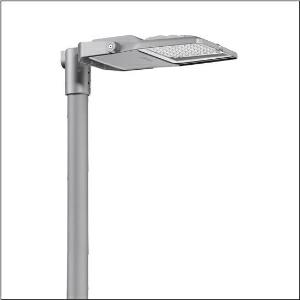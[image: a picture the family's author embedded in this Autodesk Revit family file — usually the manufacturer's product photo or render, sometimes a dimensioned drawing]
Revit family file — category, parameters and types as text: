
# Revit family: floodlight_fl_21_iq_mini___pl64_5xa7771b4e3a_3408
name_source: partatom
category: Lighting Fixtures
units: mm (PartAtom-declared; Revit-internal decimal feet)

## family parameters
Cut with Voids When Loaded = No
Host = Face
Light Source = No
Part Type = Normal
Room Calculation Point = No
Round Connector Dimension = Use Diameter
Shared = No

## types (1)
- --- (1 x LED, 6270 lm, 45.5 W, 4000K)
    Apparent Load = 46 VA
    CIE Flux Codes = 28 80 98 100 100
    Color Rendering = 70
    Color Temperature = 4000K
    Default Elevation = 1800 mm
    Description = Floodlight FL 21 iQ mini, floodlight, primary light control with lens, of PMMA, primary optical cover: protective disc, of toughened safety glass, transparent, light distribution: PL64, light emission: direct distribution, installation type: surface-mounted, LED, High Power LED, rated luminous flux: 6.270lm, luminous efficacy: 138lm/W, light colour: 740, colour temperature: 4000K, control: Auto-Match, Temp-Guard, Lumen-Switch, Night-Set, Smart-Wire, Light-Fading, Desk-Remote (wireless, voltage-free reading and setting of iQ features in the workshop via application-optimized NFC function/RFID function), optimised constant luminous flux control (CLO 2.0), with terminal, 6-pole, mains connection: 220..240V, AC, 50/60Hz, start of lifetime: 46W, end of service life: 48W, reduction: 22W, luminaire housing, of diecast aluminium, powder-coated, Siteco® metallic grey (DB 702S), corrosivity category C5 mid according to DIN EN ISO 12944, sealing non-destructively replaceable, please order mast flange separately, mast bracket, of steel, galvanised, powder-coated, Siteco® metallic grey (DB 702S), protection rating (complete): IP66, insulation class (complete): insulation class II (safety insulation), certification: CE, ENEC, VDE, protection symbol: D, impact resistance: IK08, permissible operating ambient temperature: -40..+40°C, permissible operating ambient temperature for outdoor applications: -40..+50°C, standard: DIN EN 12944, LABS conformity tested according to VDMA 24364:2018-05, packaging unit: 1 piece

Light Distribution: PL64
    Height = 70 mm
    Lamp = 1 x LED
    Lamp Light Flux = 6270 lm
    Lamp Power = 45.5 W
    Lamp count = 1
    Length = 485 mm
    Luminous efficacy = 138 lm/W
    Manufacturer = Siteco
    ModVariant = No
    Model = 5XA7771B4E3A
    Number of Poles = 1
    OnlyDefault = Yes
    Power Factor = 1
    Product Name = Floodlight FL 21 iQ mini | PL64
    Product group = floodlight | pylon annexe
    ProductGroupID = 6200
    Protection Class = Protection class II
    Protection Degree = IP 66
    RLX_Detail_Level = 1
    RLX_Emergency_Light_Flux = 0 lm
    RLX_Emergency_Type = 0
    RLX_Emergency_Type_DB = No
    RlxData = <blob elided: 101309 chars, md5=3e97cf1d>
    Socket = socket
    Standby Power = 0 W
    System Light Flux = 6270 lm
    System Power = 46 W
    Type Comments = factory setting: luminous flux: 100 % | dim-lin: 254 | 463 mA
    Type Image = l_1007125.jpg
    URL = http://relux.com
    VarID = @adj_117197
    Voltage = 0 V
    Weight = 0.00 kg
    Width = 337 mm

## geometry (parser evidence)
native form markers: Blend x4, Sweep x12
no freeform markers — native parametric forms only
